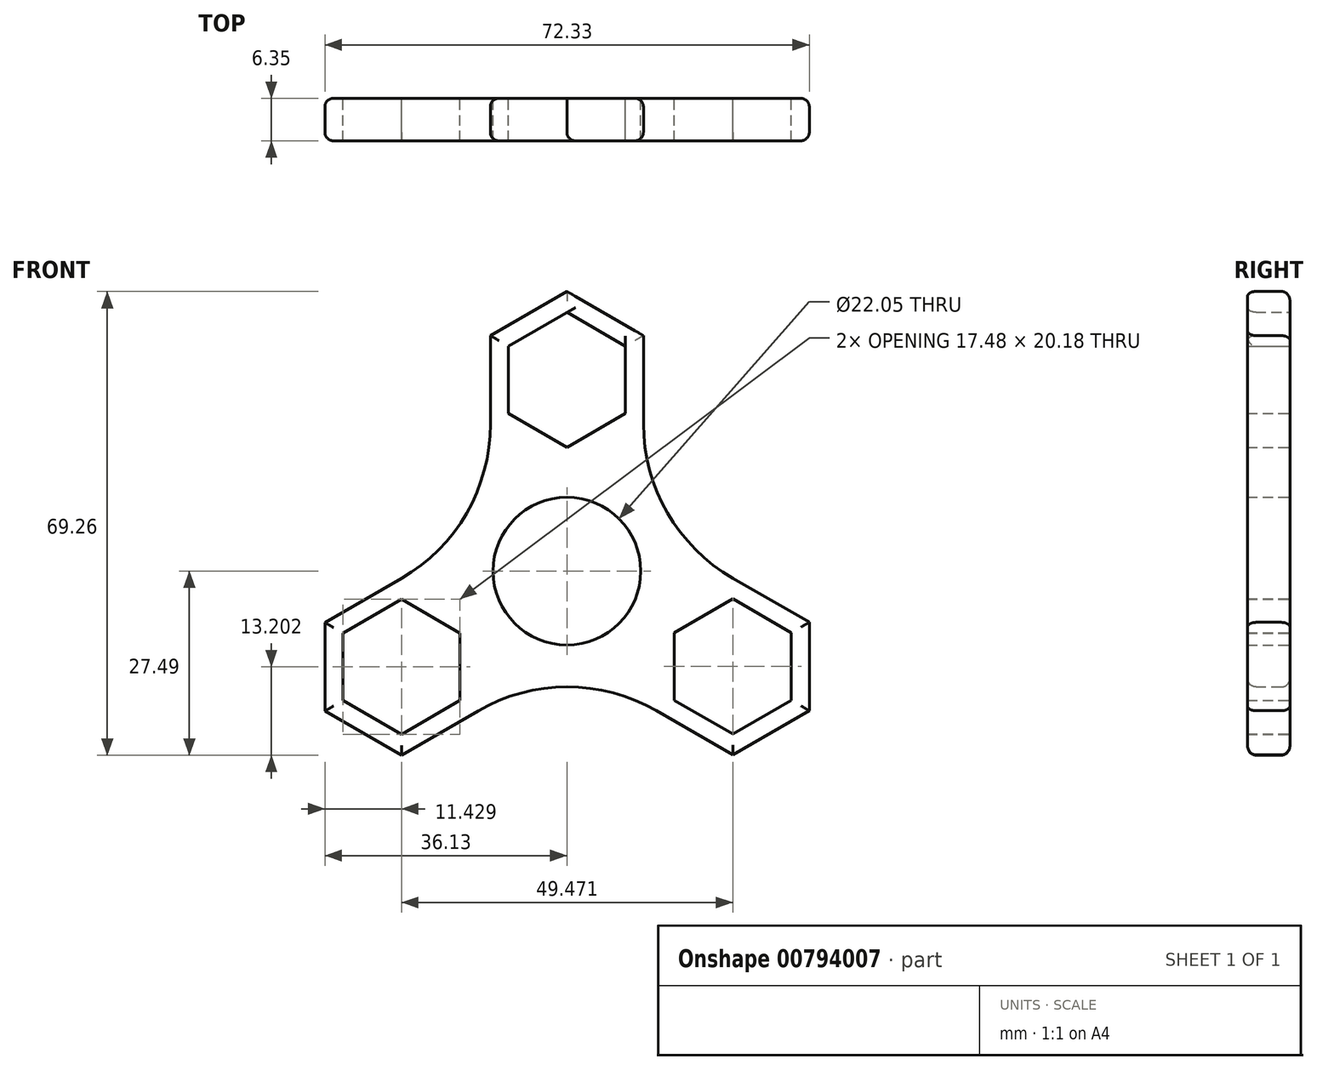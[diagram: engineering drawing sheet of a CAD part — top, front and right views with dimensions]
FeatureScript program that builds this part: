
annotation { "Feature Type Name" : "Feature", "Feature Type Description" : "" }
export const myFeature = defineFeature(function(context is Context, id is Id, definition is map)
    precondition{}
    {
        {
            var Q0;
            Q0=qCreatedBy(makeId("Front.planeOp"),FACE);
            var sketch = newSketch(context, id + "F0", { "sketchPlane" : qUnion([Q0])});
            skCircle(sketch, "E0", {"center": v(0, 0) * mm, "radius": 11.02 * mm});
            skCircle(sketch, "E1", {"center": v(0, 0) * mm, "radius": 14.29 * mm});
            skCircle(sketch, "E2.cCircle", {"center": v(0, 28.58) * mm, "radius": 8.74 * mm, "construction": true});
            skLineSegment(sketch, "E2.0", {"start": v(-8.74, 23.53) * mm, "end": v(-8.74, 33.62) * mm});
            skLineSegment(sketch, "E2.1", {"start": v(-8.74, 33.62) * mm, "end": v(0, 38.66) * mm});
            skLineSegment(sketch, "E2.2", {"start": v(0, 38.66) * mm, "end": v(8.74, 33.62) * mm});
            skLineSegment(sketch, "E2.3", {"start": v(8.74, 33.62) * mm, "end": v(8.74, 23.53) * mm});
            skLineSegment(sketch, "E2.4", {"start": v(8.74, 23.53) * mm, "end": v(0, 18.49) * mm});
            skLineSegment(sketch, "E2.5", {"start": v(0, 18.49) * mm, "end": v(-8.74, 23.53) * mm});
            skPoint(sketch, "E2.0.midPoint", {"position": v(-8.74, 28.58) * mm});
            skCircle(sketch, "E3.cCircle", {"center": v(0, 28.58) * mm, "radius": 11.43 * mm, "construction": true});
            skLineSegment(sketch, "E3.0", {"start": v(-11.43, 21.98) * mm, "end": v(-11.43, 35.17) * mm});
            skLineSegment(sketch, "E3.1", {"start": v(-11.43, 35.17) * mm, "end": v(0, 41.77) * mm});
            skLineSegment(sketch, "E3.2", {"start": v(0, 41.77) * mm, "end": v(11.43, 35.17) * mm});
            skLineSegment(sketch, "E3.3", {"start": v(11.43, 35.17) * mm, "end": v(11.43, 21.98) * mm});
            skLineSegment(sketch, "E3.4", {"start": v(11.43, 21.98) * mm, "end": v(0, 15.38) * mm});
            skLineSegment(sketch, "E3.5", {"start": v(0, 15.38) * mm, "end": v(-11.43, 21.98) * mm});
            skPoint(sketch, "E3.0.midPoint", {"position": v(-11.43, 28.58) * mm});
            skPoint(sketch, "E4.1.0", {"position": v(-18.99, -24.19) * mm});
            skCircle(sketch, "E4.1.1", {"center": v(-24.7, -14.29) * mm, "radius": 8.74 * mm, "construction": true});
            skLineSegment(sketch, "E4.1.2", {"start": v(-33.44, -19.33) * mm, "end": v(-33.44, -9.24) * mm});
            skLineSegment(sketch, "E4.1.3", {"start": v(-13.27, -7.69) * mm, "end": v(-13.27, -20.89) * mm});
            skLineSegment(sketch, "E4.1.4", {"start": v(-24.7, -1.09) * mm, "end": v(-13.27, -7.69) * mm});
            skLineSegment(sketch, "E4.1.5", {"start": v(-36.13, -7.69) * mm, "end": v(-24.7, -1.09) * mm});
            skLineSegment(sketch, "E4.1.6", {"start": v(-24.7, -24.38) * mm, "end": v(-33.44, -19.33) * mm});
            skLineSegment(sketch, "E4.1.7", {"start": v(-33.44, -9.24) * mm, "end": v(-24.7, -4.2) * mm});
            skLineSegment(sketch, "E4.1.8", {"start": v(-15.96, -9.24) * mm, "end": v(-15.96, -19.33) * mm});
            skCircle(sketch, "E4.1.9", {"center": v(-24.7, -14.29) * mm, "radius": 11.43 * mm, "construction": true});
            skLineSegment(sketch, "E4.1.10", {"start": v(-13.27, -20.89) * mm, "end": v(-24.7, -27.49) * mm});
            skLineSegment(sketch, "E4.1.11", {"start": v(-24.7, -27.49) * mm, "end": v(-36.13, -20.89) * mm});
            skLineSegment(sketch, "E4.1.12", {"start": v(-36.13, -20.89) * mm, "end": v(-36.13, -7.69) * mm});
            skPoint(sketch, "E4.1.13", {"position": v(-20.33, -21.85) * mm});
            skLineSegment(sketch, "E4.1.14", {"start": v(-15.96, -19.33) * mm, "end": v(-24.7, -24.38) * mm});
            skLineSegment(sketch, "E4.1.15", {"start": v(-24.7, -4.2) * mm, "end": v(-15.96, -9.24) * mm});
            skPoint(sketch, "E4.2.0", {"position": v(30.48, -4.35) * mm});
            skCircle(sketch, "E4.2.1", {"center": v(24.77, -14.25) * mm, "radius": 8.74 * mm, "construction": true});
            skLineSegment(sketch, "E4.2.2", {"start": v(33.5, -19.3) * mm, "end": v(24.77, -24.34) * mm});
            skLineSegment(sketch, "E4.2.3", {"start": v(13.34, -7.65) * mm, "end": v(24.77, -1.05) * mm});
            skLineSegment(sketch, "E4.2.4", {"start": v(13.34, -20.85) * mm, "end": v(13.34, -7.65) * mm});
            skLineSegment(sketch, "E4.2.5", {"start": v(24.77, -27.45) * mm, "end": v(13.34, -20.85) * mm});
            skLineSegment(sketch, "E4.2.6", {"start": v(33.5, -9.2) * mm, "end": v(33.5, -19.3) * mm});
            skLineSegment(sketch, "E4.2.7", {"start": v(24.77, -24.34) * mm, "end": v(16.03, -19.3) * mm});
            skLineSegment(sketch, "E4.2.8", {"start": v(16.03, -9.2) * mm, "end": v(24.77, -4.16) * mm});
            skCircle(sketch, "E4.2.9", {"center": v(24.77, -14.25) * mm, "radius": 11.43 * mm, "construction": true});
            skLineSegment(sketch, "E4.2.10", {"start": v(24.77, -1.05) * mm, "end": v(36.2, -7.65) * mm});
            skLineSegment(sketch, "E4.2.11", {"start": v(36.2, -7.65) * mm, "end": v(36.2, -20.85) * mm});
            skLineSegment(sketch, "E4.2.12", {"start": v(36.2, -20.85) * mm, "end": v(24.77, -27.45) * mm});
            skPoint(sketch, "E4.2.13", {"position": v(29.14, -6.68) * mm});
            skLineSegment(sketch, "E4.2.14", {"start": v(24.77, -4.16) * mm, "end": v(33.5, -9.2) * mm});
            skLineSegment(sketch, "E4.2.15", {"start": v(16.03, -19.3) * mm, "end": v(16.03, -9.2) * mm});
            skPoint(sketch, "E4.center", {"position": v(0.02, 0.01) * mm});
            skArc(sketch, "E5", {"start": v(-24.7, -1.09) * mm, "mid": v(-14.97, 8.66) * mm, "end": v(-11.43, 21.98) * mm});
            skArc(sketch, "E6", {"start": v(11.43, 21.98) * mm, "mid": v(15.02, 8.68) * mm, "end": v(24.77, -1.05) * mm});
            skArc(sketch, "E7", {"start": v(13.34, -20.85) * mm, "mid": v(0.03, -17.3) * mm, "end": v(-13.27, -20.89) * mm});
            skSolve(sketch);
        }
        {
            var Q0;
            Q0=qSketchRegion(id+"F0",true);
            var Q1;
            Q1=makeQuery(id+"F0.imprint","IMPRINT",FACE,{"disambiguationData":[TD([[makeQuery(id+"F0.imprint","IMPRINT",EDGE,{"derivedFrom":sQuery(id+"F0.wireOp",EDGE,"E0")}),-1.0]])]});
            extrude(context, id + "F1", {"entities" : qUnion([Q0, Q1]), "depth" : 6.35 * mm, "offsetDistance" : 25.4 * mm});
        }
        {
            var Q0;
            Q0=makeQuery(id+"F1.opExtrude","CAP_EDGE",EDGE,{"disambiguationData":[OSD([sQuery(id+"F0.wireOp",EDGE,"E3.1")])],"isStart":false});
            var Q1;
            Q1=makeQuery(id+"F1.opExtrude","CAP_EDGE",EDGE,{"disambiguationData":[OSD([sQuery(id+"F0.wireOp",EDGE,"E2.2")])],"isStart":false});
            var Q2;
            Q2=makeQuery(id+"F1.opExtrude","CAP_EDGE",EDGE,{"disambiguationData":[OSD([sQuery(id+"F0.wireOp",EDGE,"E3.3")])],"isStart":false});
            var Q3;
            Q3=makeQuery(id+"F1.opExtrude","CAP_EDGE",EDGE,{"disambiguationData":[OSD([sQuery(id+"F0.wireOp",EDGE,"E3.0")])],"isStart":false});
            var Q4;
            Q4=makeQuery(id+"F1.opExtrude","CAP_EDGE",EDGE,{"disambiguationData":[OSD([sQuery(id+"F0.wireOp",EDGE,"E4.2.10")])],"isStart":false});
            var Q5;
            Q5=makeQuery(id+"F1.opExtrude","CAP_EDGE",EDGE,{"disambiguationData":[OSD([sQuery(id+"F0.wireOp",EDGE,"E4.2.11")])],"isStart":false});
            var Q6;
            Q6=makeQuery(id+"F1.opExtrude","CAP_EDGE",EDGE,{"disambiguationData":[OSD([sQuery(id+"F0.wireOp",EDGE,"E4.2.12")])],"isStart":false});
            var Q7;
            Q7=makeQuery(id+"F1.opExtrude","CAP_EDGE",EDGE,{"disambiguationData":[OSD([sQuery(id+"F0.wireOp",EDGE,"E4.2.5")])],"isStart":false});
            var Q8;
            Q8=makeQuery(id+"F1.opExtrude","CAP_EDGE",EDGE,{"disambiguationData":[OSD([sQuery(id+"F0.wireOp",EDGE,"E4.1.10")])],"isStart":false});
            var Q9;
            Q9=makeQuery(id+"F1.opExtrude","CAP_EDGE",EDGE,{"disambiguationData":[OSD([sQuery(id+"F0.wireOp",EDGE,"E4.1.11")])],"isStart":false});
            var Q10;
            Q10=makeQuery(id+"F1.opExtrude","CAP_EDGE",EDGE,{"disambiguationData":[OSD([sQuery(id+"F0.wireOp",EDGE,"E4.1.12")])],"isStart":false});
            var Q11;
            Q11=makeQuery(id+"F1.opExtrude","CAP_EDGE",EDGE,{"disambiguationData":[OSD([sQuery(id+"F0.wireOp",EDGE,"E4.1.5")])],"isStart":false});
            var Q12;
            Q12=makeQuery(id+"F1.opExtrude","CAP_EDGE",EDGE,{"disambiguationData":[OSD([sQuery(id+"F0.wireOp",EDGE,"E3.0")])],"isStart":true});
            var Q13;
            Q13=makeQuery(id+"F1.opExtrude","CAP_EDGE",EDGE,{"disambiguationData":[OSD([sQuery(id+"F0.wireOp",EDGE,"E3.1")])],"isStart":true});
            var Q14;
            Q14=makeQuery(id+"F1.opExtrude","CAP_EDGE",EDGE,{"disambiguationData":[OSD([sQuery(id+"F0.wireOp",EDGE,"E3.2")])],"isStart":true});
            var Q15;
            Q15=makeQuery(id+"F1.opExtrude","CAP_EDGE",EDGE,{"disambiguationData":[OSD([sQuery(id+"F0.wireOp",EDGE,"E3.3")])],"isStart":true});
            var Q16;
            Q16=makeQuery(id+"F1.opExtrude","CAP_EDGE",EDGE,{"disambiguationData":[OSD([sQuery(id+"F0.wireOp",EDGE,"E4.2.10")])],"isStart":true});
            var Q17;
            Q17=makeQuery(id+"F1.opExtrude","CAP_EDGE",EDGE,{"disambiguationData":[OSD([sQuery(id+"F0.wireOp",EDGE,"E4.2.11")])],"isStart":true});
            var Q18;
            Q18=makeQuery(id+"F1.opExtrude","CAP_EDGE",EDGE,{"disambiguationData":[OSD([sQuery(id+"F0.wireOp",EDGE,"E4.2.12")])],"isStart":true});
            var Q19;
            Q19=makeQuery(id+"F1.opExtrude","CAP_EDGE",EDGE,{"disambiguationData":[OSD([sQuery(id+"F0.wireOp",EDGE,"E4.2.5")])],"isStart":true});
            var Q20;
            Q20=makeQuery(id+"F1.opExtrude","CAP_EDGE",EDGE,{"disambiguationData":[OSD([sQuery(id+"F0.wireOp",EDGE,"E4.1.10")])],"isStart":true});
            var Q21;
            Q21=makeQuery(id+"F1.opExtrude","CAP_EDGE",EDGE,{"disambiguationData":[OSD([sQuery(id+"F0.wireOp",EDGE,"E4.1.11")])],"isStart":true});
            var Q22;
            Q22=makeQuery(id+"F1.opExtrude","CAP_EDGE",EDGE,{"disambiguationData":[OSD([sQuery(id+"F0.wireOp",EDGE,"E4.1.12")])],"isStart":true});
            var Q23;
            Q23=makeQuery(id+"F1.opExtrude","CAP_EDGE",EDGE,{"disambiguationData":[OSD([sQuery(id+"F0.wireOp",EDGE,"E4.1.5")])],"isStart":true});
            fillet(context, id + "F2", {"entities" : qUnion([Q0, Q1, Q2, Q3, Q4, Q5, Q6, Q7, Q8, Q9, Q10, Q11, Q12, Q13, Q14, Q15, Q16, Q17, Q18, Q19, Q20, Q21, Q22, Q23]), "radius" : 1.27 * mm, "tangentPropagation" : true, "allowEdgeOverflow" : false});
        }
    });
